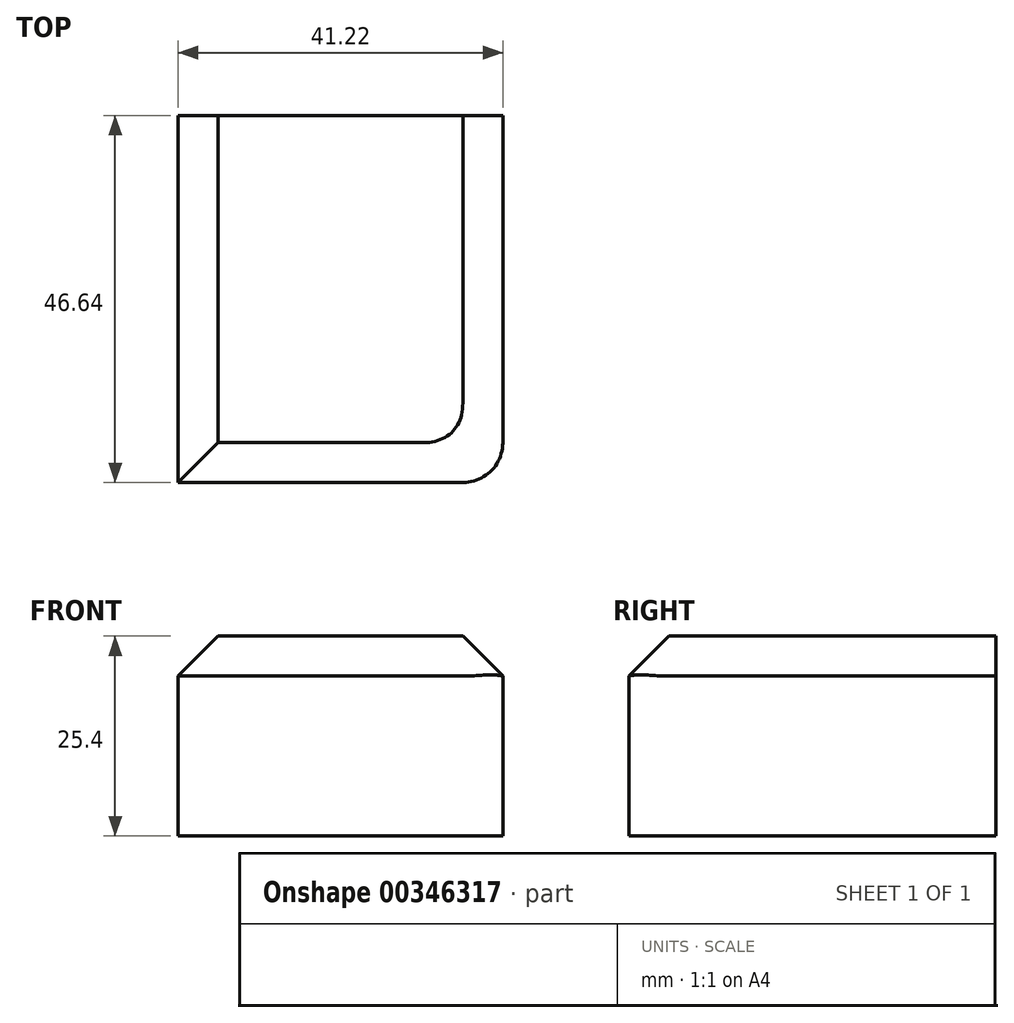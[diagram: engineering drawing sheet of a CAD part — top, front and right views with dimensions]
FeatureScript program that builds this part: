
annotation { "Feature Type Name" : "Feature", "Feature Type Description" : "" }
export const myFeature = defineFeature(function(context is Context, id is Id, definition is map)
    precondition{}
    {
        {
            var Q0;
            Q0=qCreatedBy(makeId("Top.planeOp"),FACE);
            var sketch = newSketch(context, id + "F0", { "sketchPlane" : qUnion([Q0])});
            skLineSegment(sketch, "E0.bottom", {"start": v(20.6, 23.32) * mm, "end": v(-20.6, 23.32) * mm});
            skLineSegment(sketch, "E0.top", {"start": v(20.6, -23.32) * mm, "end": v(-20.6, -23.32) * mm});
            skLineSegment(sketch, "E0.left", {"start": v(20.6, 23.32) * mm, "end": v(20.6, -23.32) * mm});
            skLineSegment(sketch, "E0.right", {"start": v(-20.6, 23.32) * mm, "end": v(-20.6, -23.32) * mm});
            skPoint(sketch, "E0.middle", {"position": v(0, 0) * mm});
            skSolve(sketch);
        }
        {
            var Q0;
            Q0=makeQuery(id+"F0.imprint","IMPRINT",FACE,{"disambiguationData":[TD([[makeQuery(id+"F0.imprint","IMPRINT",EDGE,{"derivedFrom":sQuery(id+"F0.wireOp",EDGE,"E0.bottom")}),1.0]])]});
            extrude(context, id + "F1", {"entities" : qUnion([Q0]), "depth" : 25.4 * mm});
        }
        {
            var Q0;
            Q0=makeQuery(id+"F1.opExtrude","CAP_EDGE",EDGE,{"disambiguationData":[OSD([sQuery(id+"F0.wireOp",EDGE,"E0.left")])],"isStart":false});
            var Q1;
            Q1=makeQuery(id+"F1.opExtrude","CAP_EDGE",EDGE,{"disambiguationData":[OSD([sQuery(id+"F0.wireOp",EDGE,"E0.right")])],"isStart":false});
            var Q2;
            Q2=makeQuery(id+"F1.opExtrude","CAP_EDGE",EDGE,{"disambiguationData":[OSD([sQuery(id+"F0.wireOp",EDGE,"E0.top")])],"isStart":false});
            chamfer(context, id + "F2", {"entities" : qUnion([Q0, Q1, Q2]), "width" : 5.08 * mm, "tangentPropagation" : true});
        }
        {
            var Q0;
            Q0=makeQuery(id+"F2.opChamfer","BLEND_EDGE",EDGE,{"blendedFrom":[makeQuery(id+"F1.opExtrude","CAP_EDGE",EDGE,{"disambiguationData":[OSD([sQuery(id+"F0.wireOp",EDGE,"E0.top")])],"isStart":false}),makeQuery(id+"F1.opExtrude","CAP_EDGE",EDGE,{"disambiguationData":[OSD([sQuery(id+"F0.wireOp",EDGE,"E0.left")])],"isStart":false})],"blendedInto":[]});
            fillet(context, id + "F3", {"entities" : qUnion([Q0]), "radius" : 7.11 * mm, "tangentPropagation" : true, "allowEdgeOverflow" : false});
        }
        {
            var Q0;
            Q0=makeQuery(id+"F1.opExtrude","SWEPT_EDGE",EDGE,{"disambiguationData":[OSD([sQuery(id+"F0.wireOp",EDGE,"E0.top"),sQuery(id+"F0.wireOp",EDGE,"E0.left")])]});
            fillet(context, id + "F4", {"entities" : qUnion([Q0]), "radius" : 5.08 * mm, "tangentPropagation" : true, "allowEdgeOverflow" : false});
        }
    });
